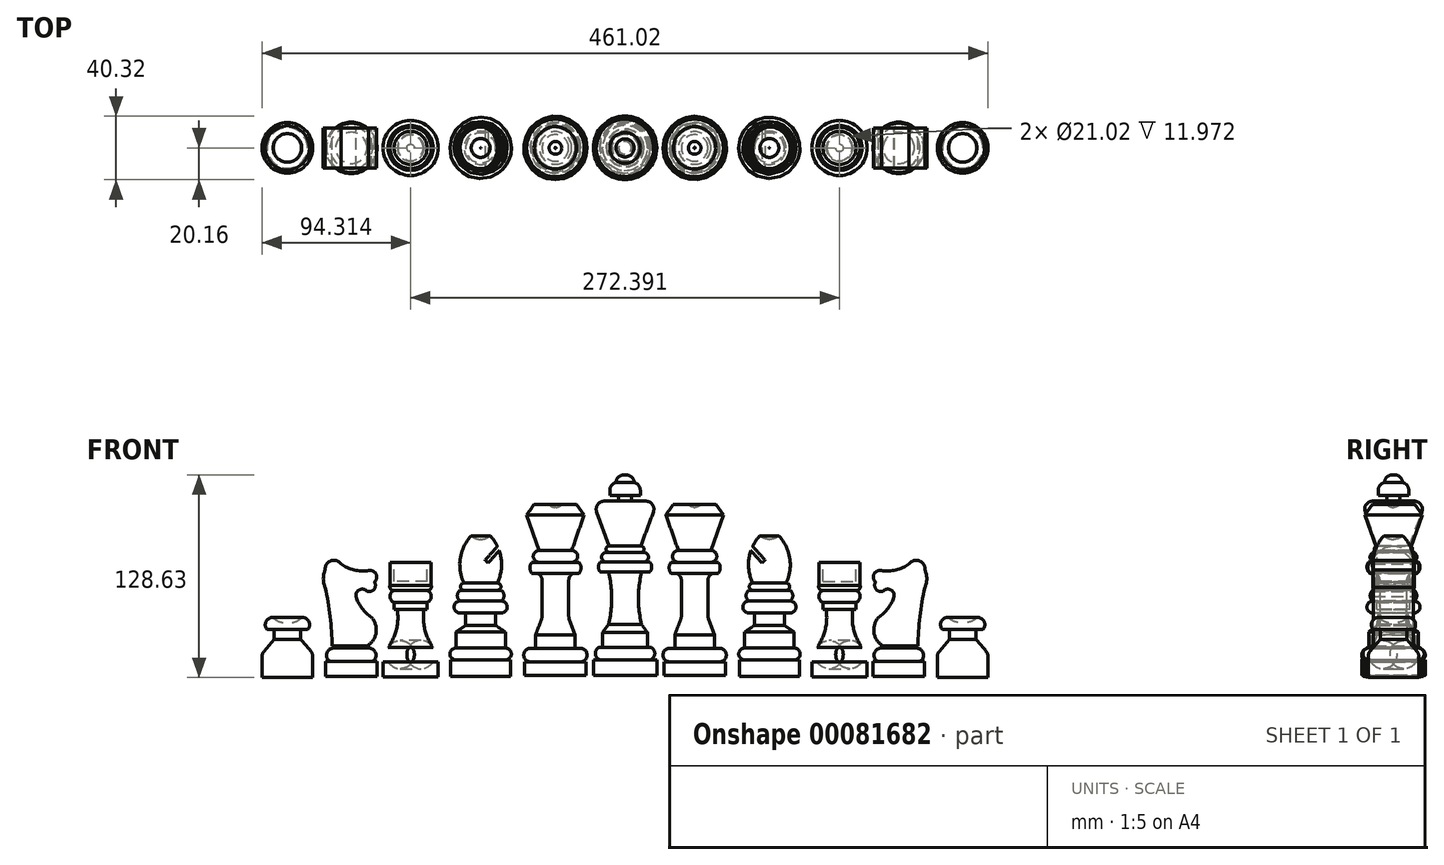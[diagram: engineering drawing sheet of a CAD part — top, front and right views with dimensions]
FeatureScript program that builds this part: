
annotation { "Feature Type Name" : "Feature", "Feature Type Description" : "" }
export const myFeature = defineFeature(function(context is Context, id is Id, definition is map)
    precondition{}
    {
        {
            var Q0;
            Q0=qCreatedBy(makeId("Front.planeOp"),FACE);
            var sketch = newSketch(context, id + "F0", { "sketchPlane" : qUnion([Q0])});
            skLineSegment(sketch, "E0", {"start": v(0, -36.85) * mm, "end": v(20.16, -36.85) * mm});
            skLineSegment(sketch, "E1", {"start": v(20.16, -36.85) * mm, "end": v(20.16, -26.8) * mm});
            skLineSegment(sketch, "E2", {"start": v(20.16, -26.8) * mm, "end": v(16.29, -26.8) * mm});
            skArc(sketch, "E3", {"start": v(16.29, -26.8) * mm, "mid": v(18.88, -22.85) * mm, "end": v(16.29, -18.9) * mm});
            skLineSegment(sketch, "E4", {"start": v(16.29, -18.9) * mm, "end": v(14.28, -18.9) * mm});
            skLineSegment(sketch, "E5", {"start": v(14.28, -18.9) * mm, "end": v(14.28, -9.47) * mm});
            skLineSegment(sketch, "E6", {"start": v(14.28, -9.47) * mm, "end": v(10.57, -4.52) * mm});
            skArc(sketch, "E7", {"start": v(10.57, 28.9) * mm, "mid": v(8.5, 12.19) * mm, "end": v(10.57, -4.52) * mm});
            skLineSegment(sketch, "E8", {"start": v(10.57, 28.9) * mm, "end": v(15.83, 28.9) * mm});
            skArc(sketch, "E9", {"start": v(15.83, 28.9) * mm, "mid": v(16.9, 32.07) * mm, "end": v(15.83, 35.24) * mm});
            skLineSegment(sketch, "E10", {"start": v(15.83, 35.24) * mm, "end": v(11.8, 35.24) * mm});
            skArc(sketch, "E11", {"start": v(11.8, 35.24) * mm, "mid": v(14.9, 38.33) * mm, "end": v(11.8, 41.42) * mm});
            skLineSegment(sketch, "E12", {"start": v(11.8, 41.42) * mm, "end": v(10.1, 41.42) * mm});
            skArc(sketch, "E13", {"start": v(10.1, 41.42) * mm, "mid": v(12.11, 43.44) * mm, "end": v(10.1, 45.45) * mm});
            skLineSegment(sketch, "E14", {"start": v(10.1, 45.45) * mm, "end": v(20.5, 73.93) * mm});
            skLineSegment(sketch, "E15", {"start": v(20.5, 73.93) * mm, "end": v(4.05, 73.93) * mm});
            skLineSegment(sketch, "E16", {"start": v(4.05, 73.93) * mm, "end": v(4.05, 77.61) * mm});
            skLineSegment(sketch, "E17", {"start": v(4.05, 77.61) * mm, "end": v(9.7, 77.61) * mm});
            skLineSegment(sketch, "E18", {"start": v(9.7, 77.61) * mm, "end": v(9.7, 85.71) * mm});
            skLineSegment(sketch, "E19", {"start": v(9.7, 85.71) * mm, "end": v(5.77, 85.71) * mm});
            skLineSegment(sketch, "E20", {"start": v(5.77, 85.71) * mm, "end": v(5.77, 90.62) * mm});
            skLineSegment(sketch, "E21", {"start": v(5.77, 90.62) * mm, "end": v(0, 90.62) * mm});
            skLineSegment(sketch, "E22", {"start": v(0, 90.62) * mm, "end": v(0, -36.85) * mm});
            skLineSegment(sketch, "E23", {"start": v(-91.7, -37.44) * mm, "end": v(-72.68, -37.44) * mm});
            skLineSegment(sketch, "E24", {"start": v(-72.68, -37.44) * mm, "end": v(-72.68, -26.95) * mm});
            skLineSegment(sketch, "E25", {"start": v(-72.68, -26.95) * mm, "end": v(-75.96, -26.95) * mm});
            skArc(sketch, "E26", {"start": v(-75.96, -26.95) * mm, "mid": v(-72.2, -23.18) * mm, "end": v(-75.96, -19.41) * mm});
            skLineSegment(sketch, "E27", {"start": v(-75.96, -19.41) * mm, "end": v(-75.96, -9.25) * mm});
            skLineSegment(sketch, "E28", {"start": v(-75.96, -9.25) * mm, "end": v(-82.19, -4.99) * mm});
            skLineSegment(sketch, "E29", {"start": v(-82.19, -4.99) * mm, "end": v(-82.19, 2.88) * mm});
            skLineSegment(sketch, "E30", {"start": v(-82.19, 2.88) * mm, "end": v(-78.58, 2.88) * mm});
            skArc(sketch, "E31", {"start": v(-78.58, 2.88) * mm, "mid": v(-74.81, 6.65) * mm, "end": v(-78.58, 10.42) * mm});
            skArc(sketch, "E32", {"start": v(-78.58, 10.42) * mm, "mid": v(-76.84, 13.86) * mm, "end": v(-78.58, 17.3) * mm});
            skLineSegment(sketch, "E33", {"start": v(-78.58, 17.3) * mm, "end": v(-81.12, 17.3) * mm});
            skArc(sketch, "E34", {"start": v(-81.12, 17.3) * mm, "mid": v(-78.84, 19.58) * mm, "end": v(-81.12, 21.85) * mm});
            skArc(sketch, "E35", {"start": v(-81.12, 21.85) * mm, "mid": v(-78.73, 37.6) * mm, "end": v(-85.68, 51.93) * mm});
            skArc(sketch, "E36", {"start": v(-85.68, 51.93) * mm, "mid": v(-83.46, 61.6) * mm, "end": v(-91.7, 67.11) * mm});
            skLineSegment(sketch, "E37", {"start": v(-91.7, 67.11) * mm, "end": v(-91.7, -37.44) * mm});
            skLineSegment(sketch, "E38", {"start": v(-136.2, -37.72) * mm, "end": v(-118.68, -37.72) * mm});
            skLineSegment(sketch, "E39", {"start": v(-118.68, -37.72) * mm, "end": v(-118.68, -28.08) * mm});
            skLineSegment(sketch, "E40", {"start": v(-118.68, -28.08) * mm, "end": v(-121.89, -28.08) * mm});
            skArc(sketch, "E41", {"start": v(-121.89, -28.08) * mm, "mid": v(-120.66, -23.55) * mm, "end": v(-121.89, -19.03) * mm});
            skArc(sketch, "E42", {"start": v(-127.73, 5.2) * mm, "mid": v(-127.18, -7.48) * mm, "end": v(-121.89, -19.03) * mm});
            skLineSegment(sketch, "E43", {"start": v(-127.73, 5.2) * mm, "end": v(-125.68, 5.2) * mm});
            skLineSegment(sketch, "E44", {"start": v(-125.68, 5.2) * mm, "end": v(-125.68, 9.59) * mm});
            skArc(sketch, "E45", {"start": v(-125.68, 9.59) * mm, "mid": v(-123.08, 13.39) * mm, "end": v(-125.68, 17.18) * mm});
            skArc(sketch, "E46", {"start": v(-125.68, 17.18) * mm, "mid": v(-123.5, 18.08) * mm, "end": v(-123.08, 20.4) * mm});
            skPoint(sketch, "E46.endSnap0", {"position": v(-123.08, 13.39) * mm});
            skLineSegment(sketch, "E47", {"start": v(-123.08, 20.4) * mm, "end": v(-123.08, 35) * mm});
            skLineSegment(sketch, "E48", {"start": v(-123.08, 35) * mm, "end": v(-125.68, 35) * mm});
            skLineSegment(sketch, "E49", {"start": v(-125.68, 35) * mm, "end": v(-125.68, 23.02) * mm});
            skLineSegment(sketch, "E50", {"start": v(-125.68, 23.02) * mm, "end": v(-136.2, 23.02) * mm});
            skLineSegment(sketch, "E51", {"start": v(-136.2, 23.02) * mm, "end": v(-136.2, -37.72) * mm});
            skLineSegment(sketch, "E52", {"start": v(-173.86, -37.33) * mm, "end": v(-157.51, -37.33) * mm});
            skLineSegment(sketch, "E53", {"start": v(-157.51, -37.33) * mm, "end": v(-157.51, -27.99) * mm});
            skLineSegment(sketch, "E54", {"start": v(-157.51, -27.99) * mm, "end": v(-160.43, -27.99) * mm});
            skArc(sketch, "E55", {"start": v(-160.43, -27.99) * mm, "mid": v(-158.5, -22.23) * mm, "end": v(-163.94, -19.52) * mm});
            skLineSegment(sketch, "E56", {"start": v(-163.94, -19.52) * mm, "end": v(-173.86, -19.52) * mm});
            skLineSegment(sketch, "E57", {"start": v(-173.86, -19.52) * mm, "end": v(-173.86, -37.33) * mm});
            skLineSegment(sketch, "E58", {"start": v(-214.45, -38) * mm, "end": v(-198.4, -38) * mm});
            skLineSegment(sketch, "E59", {"start": v(-198.4, -38) * mm, "end": v(-198.4, -22.82) * mm});
            skLineSegment(sketch, "E60", {"start": v(-198.4, -22.82) * mm, "end": v(-205.98, -13.77) * mm});
            skLineSegment(sketch, "E61", {"start": v(-205.98, -13.77) * mm, "end": v(-205.98, -7.64) * mm});
            skLineSegment(sketch, "E62", {"start": v(-205.98, -7.64) * mm, "end": v(-201.6, -7.64) * mm});
            skArc(sketch, "E63", {"start": v(-201.6, -7.64) * mm, "mid": v(-200.87, -2.51) * mm, "end": v(-205.4, 0) * mm});
            skArc(sketch, "E64", {"start": v(-205.4, 0) * mm, "mid": v(-203.75, 11.94) * mm, "end": v(-214.45, 17.47) * mm});
            skLineSegment(sketch, "E65", {"start": v(-214.45, 17.47) * mm, "end": v(-214.45, -38) * mm});
            skSolve(sketch);
        }
        {
            var Q0;
            Q0=makeQuery(id+"F0.imprint","IMPRINT",FACE,{"disambiguationData":[TD([[makeQuery(id+"F0.imprint","IMPRINT",EDGE,{"derivedFrom":sQuery(id+"F0.wireOp",EDGE,"E0")}),1.0]])]});
            var Q1;
            Q1=sQuery(id+"F0.wireOp",EDGE,"E22");
            revolve(context, id + "F1", {"entities" : qUnion([Q0]), "axis" : qUnion([Q1]), "revolveType" : RevolveType.FULL});
        }
        {
            var Q0;
            Q0=makeQuery(id+"F0.imprint","IMPRINT",FACE,{"disambiguationData":[TD([[makeQuery(id+"F0.imprint","IMPRINT",EDGE,{"derivedFrom":sQuery(id+"F0.wireOp",EDGE,"E23")}),1.0]])]});
            var Q1;
            Q1=sQuery(id+"F0.wireOp",EDGE,"E37");
            revolve(context, id + "F2", {"entities" : qUnion([Q0]), "axis" : qUnion([Q1]), "revolveType" : RevolveType.FULL});
        }
        {
            var Q0;
            Q0=makeQuery(id+"F0.imprint","IMPRINT",FACE,{"disambiguationData":[TD([[makeQuery(id+"F0.imprint","IMPRINT",EDGE,{"derivedFrom":sQuery(id+"F0.wireOp",EDGE,"E38")}),1.0]])]});
            var Q1;
            Q1=sQuery(id+"F0.wireOp",EDGE,"E51");
            revolve(context, id + "F3", {"entities" : qUnion([Q0]), "axis" : qUnion([Q1]), "revolveType" : RevolveType.FULL});
        }
        {
            var Q0;
            Q0=makeQuery(id+"F0.imprint","IMPRINT",FACE,{"disambiguationData":[TD([[makeQuery(id+"F0.imprint","IMPRINT",EDGE,{"derivedFrom":sQuery(id+"F0.wireOp",EDGE,"E52")}),1.0]])]});
            var Q1;
            Q1=sQuery(id+"F0.wireOp",EDGE,"E57");
            revolve(context, id + "F4", {"entities" : qUnion([Q0]), "axis" : qUnion([Q1]), "revolveType" : RevolveType.FULL});
        }
        {
            var Q0;
            Q0=makeQuery(id+"F0.imprint","IMPRINT",FACE,{"disambiguationData":[TD([[makeQuery(id+"F0.imprint","IMPRINT",EDGE,{"derivedFrom":sQuery(id+"F0.wireOp",EDGE,"E58")}),1.0]])]});
            var Q1;
            Q1=sQuery(id+"F0.wireOp",EDGE,"E65");
            revolve(context, id + "F5", {"entities" : qUnion([Q0]), "axis" : qUnion([Q1]), "revolveType" : RevolveType.FULL});
        }
        {
            var Q0;
            Q0=qCreatedBy(makeId("Front.planeOp"),FACE);
            var sketch = newSketch(context, id + "F6", { "sketchPlane" : qUnion([Q0])});
            skLineSegment(sketch, "E66", {"start": v(-86.93, 34.66) * mm, "end": v(-75.52, 47.43) * mm});
            skLineSegment(sketch, "E67.0", {"start": v(-88.9, 36.4) * mm, "end": v(-77.48, 49.18) * mm});
            skLineSegment(sketch, "E68", {"start": v(-186, -18.16) * mm, "end": v(-163.9, -18.16) * mm});
            skArc(sketch, "E69", {"start": v(-163.9, -18.16) * mm, "mid": v(-158.12, -9.78) * mm, "end": v(-160.95, 0) * mm});
            skArc(sketch, "E70", {"start": v(-170.9, 13.25) * mm, "mid": v(-167.01, 5.81) * mm, "end": v(-160.95, 0) * mm});
            skArc(sketch, "E71", {"start": v(-163.9, 16.7) * mm, "mid": v(-168.7, 17.63) * mm, "end": v(-170.9, 13.25) * mm});
            skArc(sketch, "E72", {"start": v(-163.9, 16.7) * mm, "mid": v(-159.41, 17.93) * mm, "end": v(-159.11, 22.57) * mm});
            skArc(sketch, "E73", {"start": v(-159.11, 22.57) * mm, "mid": v(-158.2, 27.6) * mm, "end": v(-162.8, 29.83) * mm});
            skArc(sketch, "E74", {"start": v(-180.47, 33.97) * mm, "mid": v(-172.03, 30.19) * mm, "end": v(-162.8, 29.83) * mm});
            skArc(sketch, "E75", {"start": v(-180.47, 33.97) * mm, "mid": v(-186.94, 35.98) * mm, "end": v(-190.42, 30.17) * mm});
            skArc(sketch, "E76", {"start": v(-190.42, 30.17) * mm, "mid": v(-191.63, 24.65) * mm, "end": v(-190.42, 19.12) * mm});
            skArc(sketch, "E77", {"start": v(-186, -18.16) * mm, "mid": v(-187.3, 0.59) * mm, "end": v(-190.42, 19.12) * mm});
            skLineSegment(sketch, "E78", {"start": v(-44.22, 79.54) * mm, "end": v(-44.22, -36.8) * mm});
            skLineSegment(sketch, "E79", {"start": v(-44.22, -36.8) * mm, "end": v(-24.7, -36.8) * mm});
            skLineSegment(sketch, "E80", {"start": v(-24.7, -36.8) * mm, "end": v(-24.7, -28.18) * mm});
            skLineSegment(sketch, "E81", {"start": v(-24.7, -28.18) * mm, "end": v(-28.38, -28.18) * mm});
            skArc(sketch, "E82", {"start": v(-28.38, -28.18) * mm, "mid": v(-24.06, -23.86) * mm, "end": v(-28.38, -19.55) * mm});
            skLineSegment(sketch, "E83", {"start": v(-28.38, -19.55) * mm, "end": v(-31.7, -19.55) * mm});
            skLineSegment(sketch, "E84", {"start": v(-31.7, -19.55) * mm, "end": v(-31.7, -10.91) * mm});
            skLineSegment(sketch, "E85", {"start": v(-31.7, -10.91) * mm, "end": v(-35.75, 0) * mm});
            skLineSegment(sketch, "E86", {"start": v(-35.75, 0) * mm, "end": v(-35.75, 23.61) * mm});
            skArc(sketch, "E87", {"start": v(-29.12, 28.1) * mm, "mid": v(-33.62, 27.61) * mm, "end": v(-35.75, 23.61) * mm});
            skArc(sketch, "E88", {"start": v(-29.12, 28.1) * mm, "mid": v(-28, 31.55) * mm, "end": v(-29.12, 35) * mm});
            skLineSegment(sketch, "E89", {"start": v(-29.12, 35) * mm, "end": v(-33.9, 35) * mm});
            skArc(sketch, "E90", {"start": v(-33.9, 35) * mm, "mid": v(-30.1, 38.8) * mm, "end": v(-33.9, 42.6) * mm});
            skLineSegment(sketch, "E91", {"start": v(-33.9, 42.6) * mm, "end": v(-23.6, 71.95) * mm});
            skLineSegment(sketch, "E92", {"start": v(-23.6, 71.95) * mm, "end": v(-40.16, 71.95) * mm});
            skArc(sketch, "E93", {"start": v(-40.16, 71.95) * mm, "mid": v(-39.8, 77.02) * mm, "end": v(-44.22, 79.54) * mm});
            skLineSegment(sketch, "E94", {"start": v(-77.48, 49.18) * mm, "end": v(-75.52, 47.43) * mm});
            skLineSegment(sketch, "E95", {"start": v(-86.93, 34.66) * mm, "end": v(-88.9, 36.4) * mm});
            skSolve(sketch);
        }
        {
            var Q0;
            Q0=makeQuery(id+"F6.imprint","IMPRINT",FACE,{"disambiguationData":[TD([[makeQuery(id+"F6.imprint","IMPRINT",EDGE,{"derivedFrom":sQuery(id+"F6.wireOp",EDGE,"E68")}),1.0]])]});
            extrude(context, id + "F7", {"entities" : qUnion([Q0]), "endBound" : BoundingType.SYMMETRIC, "depth" : 25.4 * mm});
        }
        {
            var Q0;
            Q0=makeQuery(id+"F6.imprint","IMPRINT",FACE,{"disambiguationData":[TD([[makeQuery(id+"F6.imprint","IMPRINT",EDGE,{"derivedFrom":sQuery(id+"F6.wireOp",EDGE,"E78")}),1.0]])]});
            var Q1;
            Q1=sQuery(id+"F6.wireOp",EDGE,"E78");
            revolve(context, id + "F8", {"entities" : qUnion([Q0]), "axis" : qUnion([Q1]), "revolveType" : RevolveType.FULL});
        }
        {
            var Q0;
            Q0=makeQuery(id+"F6.imprint","IMPRINT",FACE,{"disambiguationData":[TD([[makeQuery(id+"F6.imprint","IMPRINT",EDGE,{"derivedFrom":sQuery(id+"F6.wireOp",EDGE,"E66")}),1.0]])]});
            extrude(context, id + "F9", {"entities" : qUnion([Q0]), "operationType" : NewBodyOperationType.REMOVE, "endBound" : BoundingType.SYMMETRIC, "oppositeDirection" : true, "depth" : 381 * mm});
        }
        {
            var Q0;
            Q0=makeQuery(id+"F7.opExtrude","SWEPT_BODY",BODY,{"disambiguationData":[OSD([sQuery(id+"F6.wireOp",EDGE,"E68"),sQuery(id+"F6.wireOp",EDGE,"E69"),sQuery(id+"F6.wireOp",EDGE,"E70"),sQuery(id+"F6.wireOp",EDGE,"E71"),sQuery(id+"F6.wireOp",EDGE,"E72"),sQuery(id+"F6.wireOp",EDGE,"E73"),sQuery(id+"F6.wireOp",EDGE,"E74"),sQuery(id+"F6.wireOp",EDGE,"E75"),sQuery(id+"F6.wireOp",EDGE,"E76"),sQuery(id+"F6.wireOp",EDGE,"E77")])]});
            var Q1;
            Q1=makeQuery(id+"F3.opRevolve","SWEPT_BODY",BODY,{"disambiguationData":[OSD([sQuery(id+"F0.wireOp",EDGE,"E38"),sQuery(id+"F0.wireOp",EDGE,"E39"),sQuery(id+"F0.wireOp",EDGE,"E40"),sQuery(id+"F0.wireOp",EDGE,"E41"),sQuery(id+"F0.wireOp",EDGE,"E42"),sQuery(id+"F0.wireOp",EDGE,"E43"),sQuery(id+"F0.wireOp",EDGE,"E44"),sQuery(id+"F0.wireOp",EDGE,"E45"),sQuery(id+"F0.wireOp",EDGE,"E46"),sQuery(id+"F0.wireOp",EDGE,"E47"),sQuery(id+"F0.wireOp",EDGE,"E48"),sQuery(id+"F0.wireOp",EDGE,"E49"),sQuery(id+"F0.wireOp",EDGE,"E50"),sQuery(id+"F0.wireOp",EDGE,"E51")])]});
            var Q2;
            Q2=makeQuery(id+"F5.opRevolve","SWEPT_BODY",BODY,{"disambiguationData":[OSD([sQuery(id+"F0.wireOp",EDGE,"E58"),sQuery(id+"F0.wireOp",EDGE,"E59"),sQuery(id+"F0.wireOp",EDGE,"E60"),sQuery(id+"F0.wireOp",EDGE,"E61"),sQuery(id+"F0.wireOp",EDGE,"E62"),sQuery(id+"F0.wireOp",EDGE,"E63"),sQuery(id+"F0.wireOp",EDGE,"E64"),sQuery(id+"F0.wireOp",EDGE,"E65")])]});
            var Q3;
            Q3=makeQuery(id+"F4.opRevolve","SWEPT_BODY",BODY,{"disambiguationData":[OSD([sQuery(id+"F0.wireOp",EDGE,"E52"),sQuery(id+"F0.wireOp",EDGE,"E53"),sQuery(id+"F0.wireOp",EDGE,"E54"),sQuery(id+"F0.wireOp",EDGE,"E55"),sQuery(id+"F0.wireOp",EDGE,"E56"),sQuery(id+"F0.wireOp",EDGE,"E57")])]});
            var Q4;
            Q4=makeQuery(id+"F8.opRevolve","SWEPT_BODY",BODY,{"disambiguationData":[OSD([sQuery(id+"F6.wireOp",EDGE,"E78"),sQuery(id+"F6.wireOp",EDGE,"E79"),sQuery(id+"F6.wireOp",EDGE,"E80"),sQuery(id+"F6.wireOp",EDGE,"E81"),sQuery(id+"F6.wireOp",EDGE,"E82"),sQuery(id+"F6.wireOp",EDGE,"E83"),sQuery(id+"F6.wireOp",EDGE,"E84"),sQuery(id+"F6.wireOp",EDGE,"E85"),sQuery(id+"F6.wireOp",EDGE,"E86"),sQuery(id+"F6.wireOp",EDGE,"E87"),sQuery(id+"F6.wireOp",EDGE,"E88"),sQuery(id+"F6.wireOp",EDGE,"E89"),sQuery(id+"F6.wireOp",EDGE,"E90"),sQuery(id+"F6.wireOp",EDGE,"E91"),sQuery(id+"F6.wireOp",EDGE,"E92"),sQuery(id+"F6.wireOp",EDGE,"E93")])]});
            var Q5;
            Q5=makeQuery(id+"F2.opRevolve","SWEPT_BODY",BODY,{"disambiguationData":[OSD([sQuery(id+"F0.wireOp",EDGE,"E23"),sQuery(id+"F0.wireOp",EDGE,"E24"),sQuery(id+"F0.wireOp",EDGE,"E25"),sQuery(id+"F0.wireOp",EDGE,"E26"),sQuery(id+"F0.wireOp",EDGE,"E27"),sQuery(id+"F0.wireOp",EDGE,"E28"),sQuery(id+"F0.wireOp",EDGE,"E29"),sQuery(id+"F0.wireOp",EDGE,"E30"),sQuery(id+"F0.wireOp",EDGE,"E31"),sQuery(id+"F0.wireOp",EDGE,"E32"),sQuery(id+"F0.wireOp",EDGE,"E33"),sQuery(id+"F0.wireOp",EDGE,"E34"),sQuery(id+"F0.wireOp",EDGE,"E35"),sQuery(id+"F0.wireOp",EDGE,"E36"),sQuery(id+"F0.wireOp",EDGE,"E37")])]});
            var Q6;
            Q6=qCreatedBy(makeId("Right.planeOp"),FACE);
            mirror(context, id + "F10", {"entities" : qUnion([Q0, Q1, Q2, Q3, Q4, Q5]), "mirrorPlane" : qUnion([Q6])});
        }
        {
            var Q0;
            Q0=makeQuery(id+"F1.opRevolve","SWEPT_EDGE",EDGE,{"disambiguationData":[OSD([sQuery(id+"F0.wireOp",EDGE,"E18"),sQuery(id+"F0.wireOp",EDGE,"E19")])]});
            var Q1;
            Q1=makeQuery(id+"F1.opRevolve","SWEPT_EDGE",EDGE,{"disambiguationData":[OSD([sQuery(id+"F0.wireOp",EDGE,"E20"),sQuery(id+"F0.wireOp",EDGE,"E21")])]});
            fillet(context, id + "F11", {"entities" : qUnion([Q0, Q1]), "radius" : 5.08 * mm, "tangentPropagation" : true, "allowEdgeOverflow" : false});
        }
        {
            var Q0;
            Q0=makeQuery(id+"F5.opRevolve","SWEPT_EDGE",EDGE,{"disambiguationData":[OSD([sQuery(id+"F0.wireOp",EDGE,"E59"),sQuery(id+"F0.wireOp",EDGE,"E60")])]});
            var Q1;
            Q1=makeQuery(id+"F10.opPattern","COPY",EDGE,{"derivedFrom":makeQuery(id+"F5.opRevolve","SWEPT_EDGE",EDGE,{"disambiguationData":[OSD([sQuery(id+"F0.wireOp",EDGE,"E59"),sQuery(id+"F0.wireOp",EDGE,"E60")])]}),"instanceName":"1"});
            fillet(context, id + "F12", {"entities" : qUnion([Q0, Q1]), "radius" : 5.08 * mm, "tangentPropagation" : true, "allowEdgeOverflow" : false});
        }
        {
            var Q0;
            Q0=makeQuery(id+"F10.opPattern","COPY",EDGE,{"derivedFrom":makeQuery(id+"F8.opRevolve","SWEPT_EDGE",EDGE,{"disambiguationData":[OSD([sQuery(id+"F6.wireOp",EDGE,"E91"),sQuery(id+"F6.wireOp",EDGE,"E92")])]}),"instanceName":"1"});
            chamfer(context, id + "F13", {"entities" : qUnion([Q0]), "width" : 5.08 * mm, "tangentPropagation" : true});
        }
        {
            var Q0;
            Q0=makeQuery(id+"F8.opRevolve","SWEPT_EDGE",EDGE,{"disambiguationData":[OSD([sQuery(id+"F6.wireOp",EDGE,"E91"),sQuery(id+"F6.wireOp",EDGE,"E92")])]});
            chamfer(context, id + "F14", {"entities" : qUnion([Q0]), "width" : 5.08 * mm, "tangentPropagation" : true});
        }
        {
            var Q0;
            Q0=makeQuery(id+"F1.opRevolve","SWEPT_EDGE",EDGE,{"disambiguationData":[OSD([sQuery(id+"F0.wireOp",EDGE,"E14"),sQuery(id+"F0.wireOp",EDGE,"E15")])]});
            fillet(context, id + "F15", {"entities" : qUnion([Q0]), "radius" : 5.08 * mm, "tangentPropagation" : true, "allowEdgeOverflow" : false});
        }
        {
            var Q0;
            Q0=makeQuery(id+"F8.opRevolve","SWEPT_EDGE",EDGE,{"disambiguationData":[OSD([sQuery(id+"F6.wireOp",EDGE,"E85"),sQuery(id+"F6.wireOp",EDGE,"E86")])]});
            fillet(context, id + "F16", {"entities" : qUnion([Q0]), "radius" : 5.08 * mm, "tangentPropagation" : true, "allowEdgeOverflow" : false});
        }
        {
            var Q0;
            Q0=makeQuery(id+"F10.opPattern","COPY",EDGE,{"derivedFrom":makeQuery(id+"F8.opRevolve","SWEPT_EDGE",EDGE,{"disambiguationData":[OSD([sQuery(id+"F6.wireOp",EDGE,"E85"),sQuery(id+"F6.wireOp",EDGE,"E86")])]}),"instanceName":"1"});
            fillet(context, id + "F17", {"entities" : qUnion([Q0]), "radius" : 5.08 * mm, "tangentPropagation" : true, "allowEdgeOverflow" : false});
        }
    });
